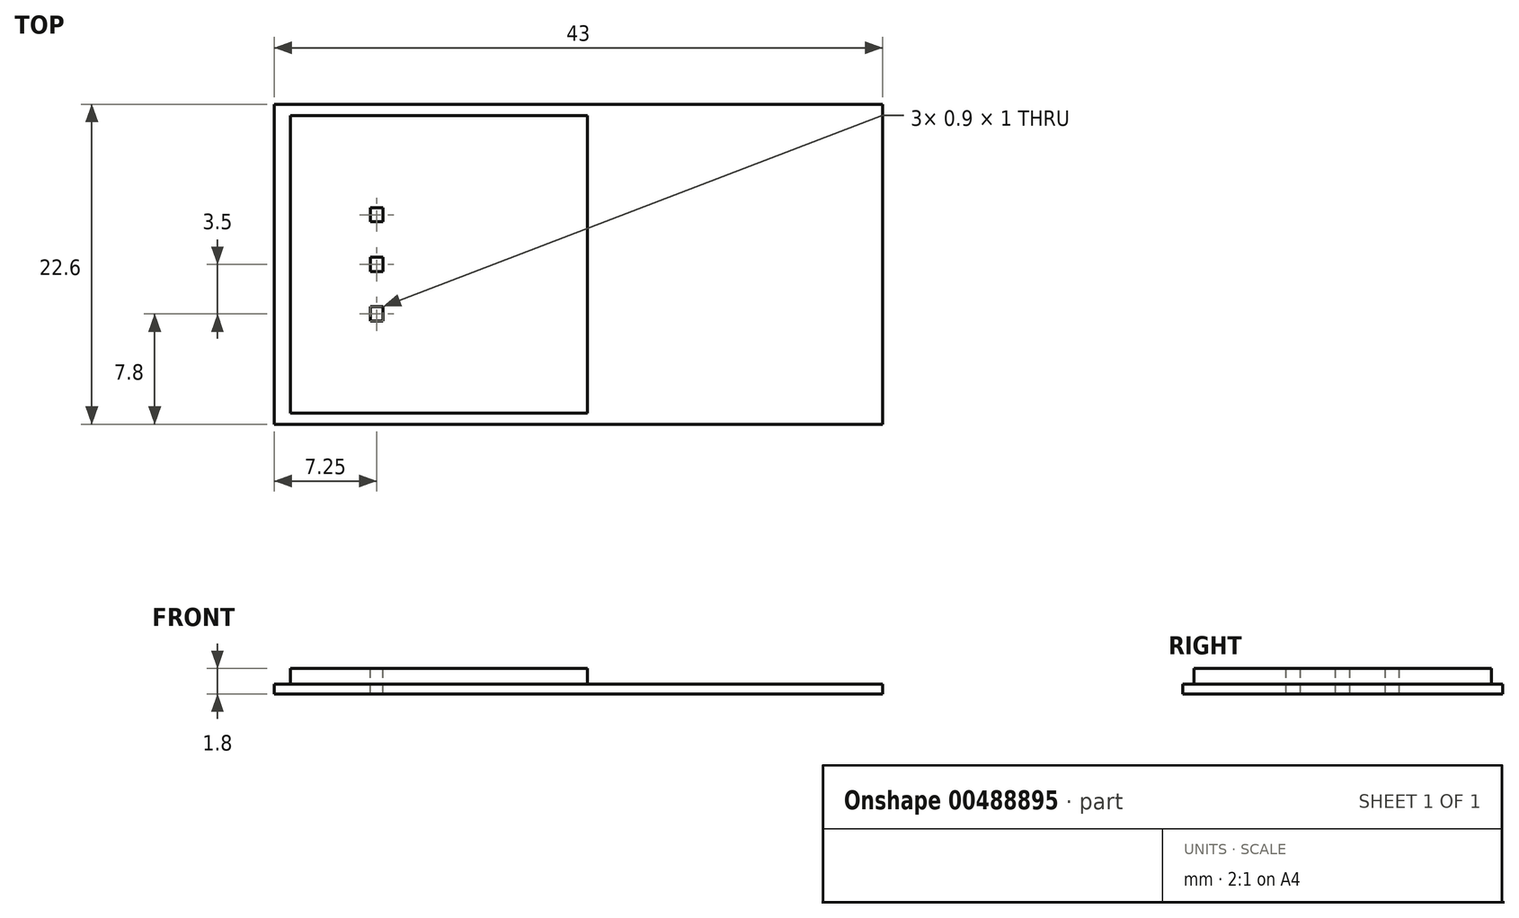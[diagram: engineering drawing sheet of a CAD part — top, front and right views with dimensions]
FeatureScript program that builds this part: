
annotation { "Feature Type Name" : "Feature", "Feature Type Description" : "" }
export const myFeature = defineFeature(function(context is Context, id is Id, definition is map)
    precondition{}
    {
        {
            var Q0;
            Q0=qCreatedBy(makeId("Top.planeOp"),FACE);
            var sketch = newSketch(context, id + "F0", { "sketchPlane" : qUnion([Q0])});
            skLineSegment(sketch, "E0.bottom", {"start": v(21.5, -11.3) * mm, "end": v(-21.5, -11.3) * mm});
            skLineSegment(sketch, "E0.top", {"start": v(21.5, 11.3) * mm, "end": v(-21.5, 11.3) * mm});
            skLineSegment(sketch, "E0.left", {"start": v(21.5, -11.3) * mm, "end": v(21.5, 11.3) * mm});
            skLineSegment(sketch, "E0.right", {"start": v(-21.5, -11.3) * mm, "end": v(-21.5, 11.3) * mm});
            skPoint(sketch, "E0.middle", {"position": v(0, 0) * mm});
            skLineSegment(sketch, "E1.bottom", {"start": v(-13.8, -0.5) * mm, "end": v(-14.7, -0.5) * mm});
            skLineSegment(sketch, "E1.top", {"start": v(-13.8, 0.5) * mm, "end": v(-14.7, 0.5) * mm});
            skLineSegment(sketch, "E1.left", {"start": v(-13.8, -0.5) * mm, "end": v(-13.8, 0.5) * mm});
            skLineSegment(sketch, "E1.right", {"start": v(-14.7, -0.5) * mm, "end": v(-14.7, 0.5) * mm});
            skPoint(sketch, "E1.middle", {"position": v(-14.25, 0) * mm});
            skLineSegment(sketch, "E2.bottom", {"start": v(-13.8, 3) * mm, "end": v(-14.7, 3) * mm});
            skLineSegment(sketch, "E2.top", {"start": v(-13.8, 4) * mm, "end": v(-14.7, 4) * mm});
            skLineSegment(sketch, "E2.left", {"start": v(-13.8, 3) * mm, "end": v(-13.8, 4) * mm});
            skLineSegment(sketch, "E2.right", {"start": v(-14.7, 3) * mm, "end": v(-14.7, 4) * mm});
            skPoint(sketch, "E2.middle", {"position": v(-14.25, 3.5) * mm});
            skLineSegment(sketch, "E3.MirrorCS", {"start": v(-13.8, -3) * mm, "end": v(-14.7, -3) * mm});
            skPoint(sketch, "E4.MirrorP", {"position": v(-14.25, -3.5) * mm});
            skLineSegment(sketch, "E5.MirrorCS", {"start": v(-14.7, -3) * mm, "end": v(-14.7, -4) * mm});
            skLineSegment(sketch, "E6.MirrorCS", {"start": v(-13.8, -3) * mm, "end": v(-13.8, -4) * mm});
            skLineSegment(sketch, "E7.MirrorCS", {"start": v(-13.8, -4) * mm, "end": v(-14.7, -4) * mm});
            skSolve(sketch);
        }
        {
            var Q0;
            Q0=makeQuery(id+"F0.imprint","IMPRINT",FACE,{"disambiguationData":[TD([[makeQuery(id+"F0.imprint","IMPRINT",EDGE,{"derivedFrom":sQuery(id+"F0.wireOp",EDGE,"E0.bottom")}),-1.0]])]});
            extrude(context, id + "F1", {"entities" : qUnion([Q0]), "oppositeDirection" : true, "depth" : 0.7 * mm});
        }
        {
            var Q0;
            Q0=makeQuery(id+"F1.opExtrude","CAP_FACE",FACE,{"disambiguationData":[OSD([sQuery(id+"F0.wireOp",EDGE,"E0.bottom"),sQuery(id+"F0.wireOp",EDGE,"E0.top"),sQuery(id+"F0.wireOp",EDGE,"E0.left"),sQuery(id+"F0.wireOp",EDGE,"E0.right"),sQuery(id+"F0.wireOp",EDGE,"E1.bottom"),sQuery(id+"F0.wireOp",EDGE,"E1.top"),sQuery(id+"F0.wireOp",EDGE,"E1.left"),sQuery(id+"F0.wireOp",EDGE,"E1.right"),sQuery(id+"F0.wireOp",EDGE,"E2.bottom"),sQuery(id+"F0.wireOp",EDGE,"E2.top"),sQuery(id+"F0.wireOp",EDGE,"E2.left"),sQuery(id+"F0.wireOp",EDGE,"E2.right"),sQuery(id+"F0.wireOp",EDGE,"E3.MirrorCS"),sQuery(id+"F0.wireOp",EDGE,"E5.MirrorCS"),sQuery(id+"F0.wireOp",EDGE,"E6.MirrorCS"),sQuery(id+"F0.wireOp",EDGE,"E7.MirrorCS")])],"isStart":true});
            var sketch = newSketch(context, id + "F2", { "sketchPlane" : qUnion([Q0])});
            skLineSegment(sketch, "E8.bottom", {"start": v(0.64, -10.5) * mm, "end": v(-20.36, -10.5) * mm});
            skLineSegment(sketch, "E8.top", {"start": v(0.64, 10.5) * mm, "end": v(-20.36, 10.5) * mm});
            skLineSegment(sketch, "E8.left", {"start": v(0.64, -10.5) * mm, "end": v(0.64, 10.5) * mm});
            skLineSegment(sketch, "E8.right", {"start": v(-20.36, -10.5) * mm, "end": v(-20.36, 10.5) * mm});
            skPoint(sketch, "E8.middle", {"position": v(-9.86, 0) * mm});
            skSolve(sketch);
        }
        {
            var Q0;
            Q0=makeQuery(id+"F2.imprint","IMPRINT",FACE,{"disambiguationData":[TD([[makeQuery(id+"F2.imprint","IMPRINT",EDGE,{"derivedFrom":sQuery(id+"F2.wireOp",EDGE,"E8.bottom")}),-1.0]])]});
            extrude(context, id + "F3", {"entities" : qUnion([Q0]), "operationType" : NewBodyOperationType.ADD, "depth" : 1.1 * mm});
        }
    });
